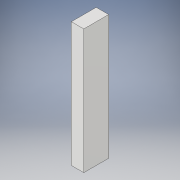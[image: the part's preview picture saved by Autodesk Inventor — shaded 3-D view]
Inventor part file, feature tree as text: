
AUTODESK INVENTOR PART (.ipt)
format: ipt  version: 2017 (Build 210142000, 142)  size: 91,136 bytes
history: native  units: in
note: dims shown in document units (in); Inventor stores cm internally (conversion verified against a paired STEP export)
features: extrude x1, sketch x1
ambient origin geometry x8: Origin, YZ Plane, XZ Plane, XY Plane, X Axis, Y Axis, Z Axis, Center Point
bodies: Solid1 (feature_tree)
feature tree (2):
  extrude  "Extrusion1"  Depth=1.5in
  sketch  "Sketch1"  dims[d0=0.75in d1=1.5in d2=7.5in d3=0.0in]
